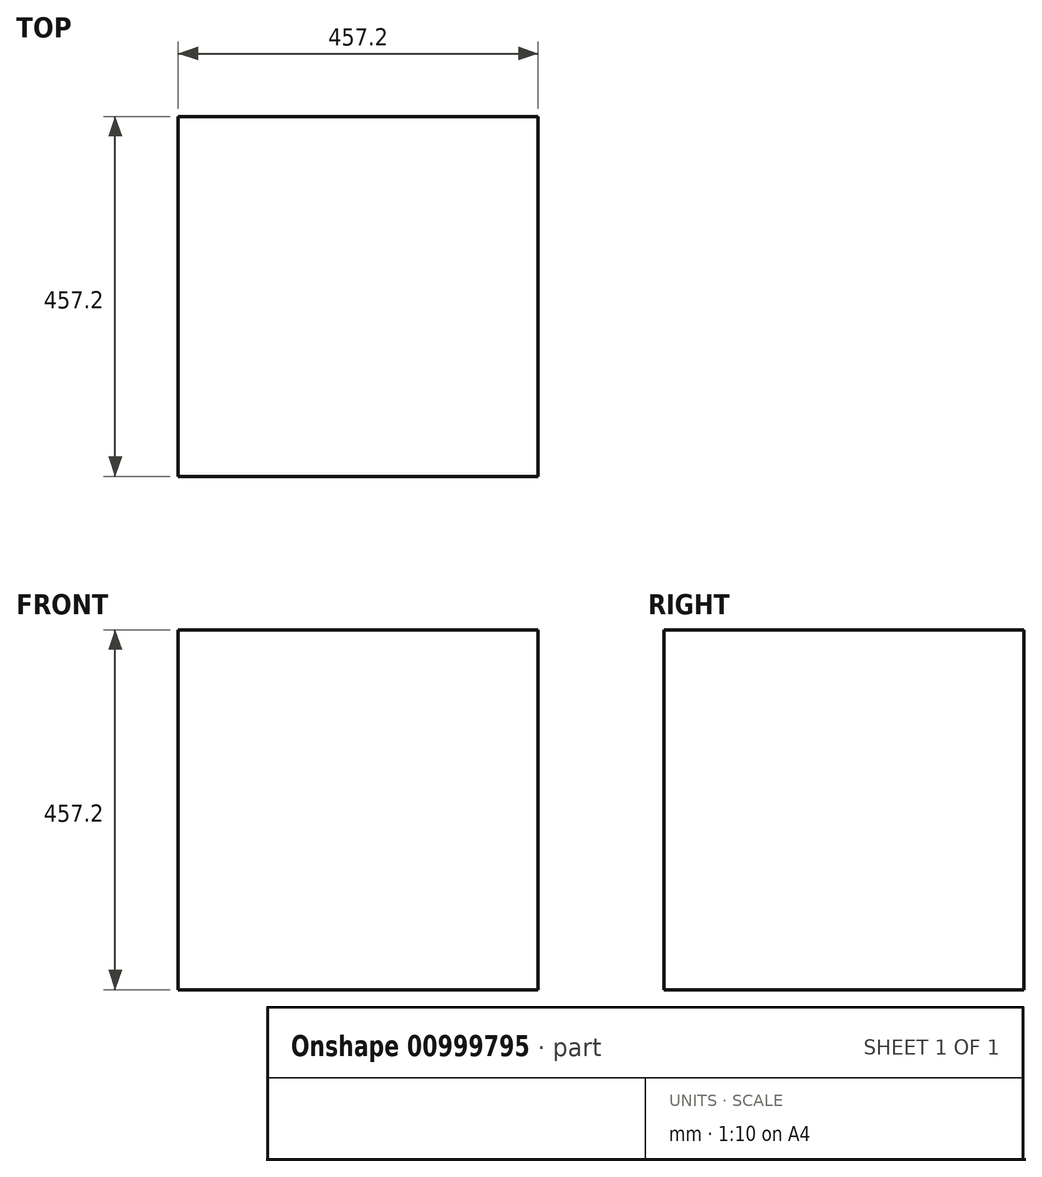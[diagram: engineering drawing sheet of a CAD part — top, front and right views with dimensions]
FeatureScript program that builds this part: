
annotation { "Feature Type Name" : "Feature", "Feature Type Description" : "" }
export const myFeature = defineFeature(function(context is Context, id is Id, definition is map)
    precondition{}
    {
        {
            var Q0;
            Q0=qCreatedBy(makeId("Right.planeOp"),FACE);
            var sketch = newSketch(context, id + "F0", { "sketchPlane" : qUnion([Q0])});
            skLineSegment(sketch, "E0.bottom", {"start": v(228.6, 228.6) * mm, "end": v(-228.6, 228.6) * mm});
            skLineSegment(sketch, "E0.top", {"start": v(228.6, -228.6) * mm, "end": v(-228.6, -228.6) * mm});
            skLineSegment(sketch, "E0.left", {"start": v(228.6, 228.6) * mm, "end": v(228.6, -228.6) * mm});
            skLineSegment(sketch, "E0.right", {"start": v(-228.6, 228.6) * mm, "end": v(-228.6, -228.6) * mm});
            skPoint(sketch, "E0.middle", {"position": v(0, 0) * mm});
            skSolve(sketch);
        }
        {
            var Q0;
            Q0=makeQuery(id+"F0.imprint","IMPRINT",FACE,{"disambiguationData":[TD([[makeQuery(id+"F0.imprint","IMPRINT",EDGE,{"derivedFrom":sQuery(id+"F0.wireOp",EDGE,"E0.bottom")}),1.0]])]});
            extrude(context, id + "F1", {"entities" : qUnion([Q0]), "depth" : 457.2 * mm, "offsetDistance" : 25.4 * mm, "symmetric" : true});
        }
    });
